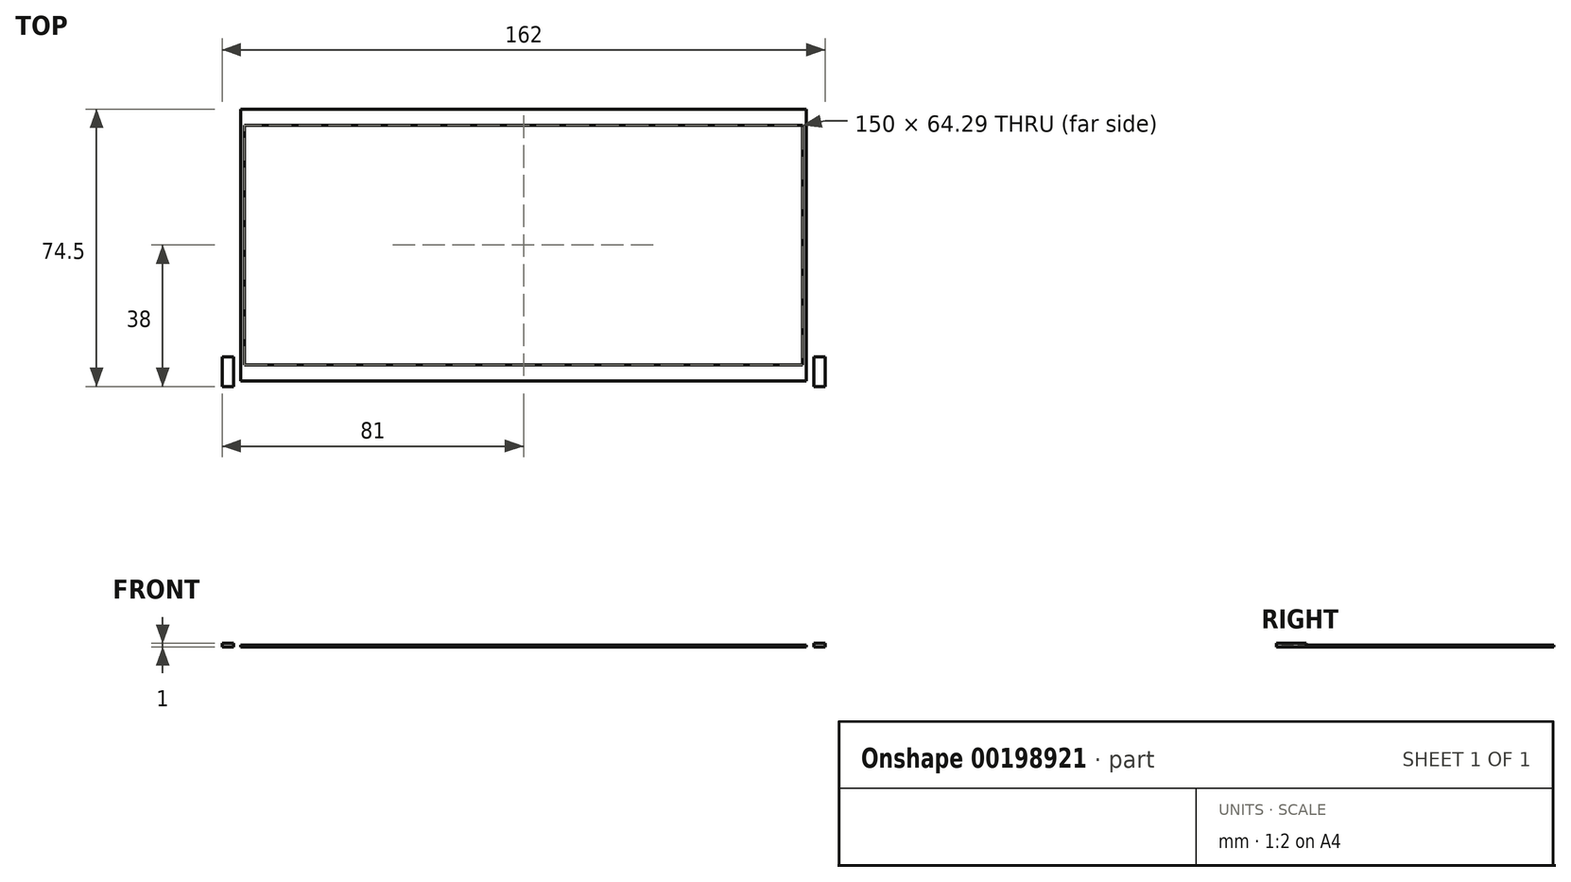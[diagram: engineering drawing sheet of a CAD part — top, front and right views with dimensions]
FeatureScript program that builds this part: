
annotation { "Feature Type Name" : "Feature", "Feature Type Description" : "" }
export const myFeature = defineFeature(function(context is Context, id is Id, definition is map)
    precondition{}
    {
        {
            var Q0;
            Q0=qCreatedBy(makeId("Top.planeOp"),FACE);
            var sketch = newSketch(context, id + "F0", { "sketchPlane" : qUnion([Q0])});
            skLineSegment(sketch, "E0.bottom", {"start": v(-81, -38) * mm, "end": v(81, -38) * mm});
            skLineSegment(sketch, "E0.top", {"start": v(-81, 38) * mm, "end": v(81, 38) * mm});
            skLineSegment(sketch, "E0.left", {"start": v(-81, -38) * mm, "end": v(-81, 38) * mm});
            skLineSegment(sketch, "E0.right", {"start": v(81, -38) * mm, "end": v(81, 38) * mm});
            skPoint(sketch, "E0.middle", {"position": v(0, 0) * mm});
            skLineSegment(sketch, "E1.bottom", {"start": v(-76, -36.5) * mm, "end": v(76, -36.5) * mm});
            skLineSegment(sketch, "E1.top", {"start": v(-76, 36.5) * mm, "end": v(76, 36.5) * mm});
            skLineSegment(sketch, "E1.left", {"start": v(-76, -36.5) * mm, "end": v(-76, 36.5) * mm});
            skLineSegment(sketch, "E1.right", {"start": v(76, -36.5) * mm, "end": v(76, 36.5) * mm});
            skLineSegment(sketch, "E2.bottom", {"start": v(-75, -32.15) * mm, "end": v(75, -32.15) * mm});
            skLineSegment(sketch, "E2.top", {"start": v(-75, 32.15) * mm, "end": v(75, 32.15) * mm});
            skLineSegment(sketch, "E2.left", {"start": v(-75, -32.15) * mm, "end": v(-75, 32.15) * mm});
            skLineSegment(sketch, "E2.right", {"start": v(75, -32.15) * mm, "end": v(75, 32.15) * mm});
            skLineSegment(sketch, "E3.bottom", {"start": v(-81, -38) * mm, "end": v(-78, -38) * mm});
            skLineSegment(sketch, "E3.top", {"start": v(-81, -30) * mm, "end": v(-78, -30) * mm});
            skLineSegment(sketch, "E3.left", {"start": v(-81, -38) * mm, "end": v(-81, -30) * mm});
            skLineSegment(sketch, "E3.right", {"start": v(-78, -38) * mm, "end": v(-78, -30) * mm});
            skLineSegment(sketch, "E4.bottom", {"start": v(81, -38) * mm, "end": v(78, -38) * mm});
            skLineSegment(sketch, "E4.top", {"start": v(81, -30) * mm, "end": v(78, -30) * mm});
            skLineSegment(sketch, "E4.left", {"start": v(81, -38) * mm, "end": v(81, -30) * mm});
            skLineSegment(sketch, "E4.right", {"start": v(78, -38) * mm, "end": v(78, -30) * mm});
            skSolve(sketch);
        }
        {
            var Q0;
            Q0=makeQuery(id+"F0.imprint","IMPRINT",FACE,{"disambiguationData":[TD([[makeQuery(id+"F0.imprint","IMPRINT",EDGE,{"derivedFrom":sQuery(id+"F0.wireOp",EDGE,"E0.bottom")}),1.0]])]});
            extrude(context, id + "F1", {"entities" : qUnion([Q0]), "depth" : 1 * mm});
        }
        {
            var Q0;
            Q0=makeQuery(id+"F0.imprint","IMPRINT",FACE,{"disambiguationData":[TD([[makeQuery(id+"F0.imprint","IMPRINT",EDGE,{"derivedFrom":sQuery(id+"F0.wireOp",EDGE,"E1.bottom")}),1.0]])]});
            extrude(context, id + "F2", {"entities" : qUnion([Q0]), "operationType" : NewBodyOperationType.ADD, "depth" : 0.5 * mm});
        }
    });
